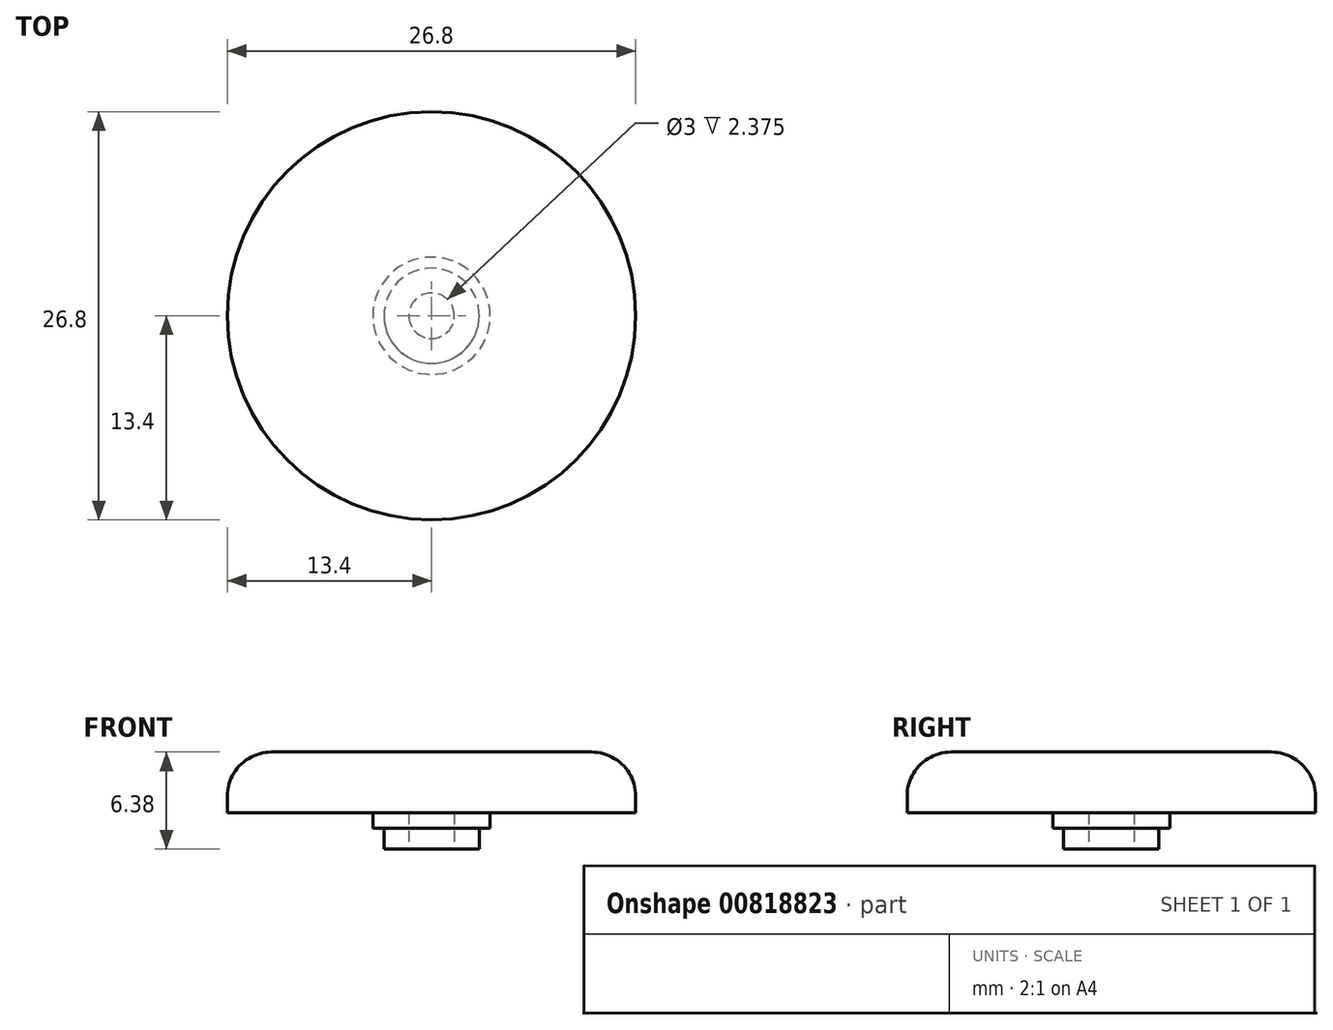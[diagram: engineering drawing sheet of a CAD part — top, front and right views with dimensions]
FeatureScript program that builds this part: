
annotation { "Feature Type Name" : "Feature", "Feature Type Description" : "" }
export const myFeature = defineFeature(function(context is Context, id is Id, definition is map)
    precondition{}
    {
        {
            var Q0;
            Q0=qCreatedBy(makeId("Top.planeOp"),FACE);
            var sketch = newSketch(context, id + "F0", { "sketchPlane" : qUnion([Q0])});
            skCircle(sketch, "E0", {"center": v(0, 0) * mm, "radius": 3.13 * mm});
            skCircle(sketch, "E1", {"center": v(0, 0) * mm, "radius": 1.5 * mm});
            skSolve(sketch);
        }
        {
            var Q0;
            Q0=makeQuery(id+"F0.imprint","IMPRINT",FACE,{"disambiguationData":[TD([[makeQuery(id+"F0.imprint","IMPRINT",EDGE,{"derivedFrom":sQuery(id+"F0.wireOp",EDGE,"E0")}),1.0]])]});
            extrude(context, id + "F1", {"entities" : qUnion([Q0]), "depth" : 2.38 * mm, "offsetDistance" : 25 * mm});
        }
        {
            var Q0;
            Q0=makeQuery(id+"F1.opExtrude","CAP_FACE",FACE,{"disambiguationData":[OSD([sQuery(id+"F0.wireOp",EDGE,"E0")])],"isStart":false});
            var sketch = newSketch(context, id + "F2", { "sketchPlane" : qUnion([Q0])});
            skCircle(sketch, "E2", {"center": v(0, 0) * mm, "radius": 13.4 * mm});
            skSolve(sketch);
        }
        {
            var Q0;
            Q0=makeQuery(id+"F2.imprint","IMPRINT",FACE,{"disambiguationData":[TD([[makeQuery(id+"F2.imprint","IMPRINT",EDGE,{"derivedFrom":sQuery(id+"F2.wireOp",EDGE,"E2")}),1.0]])]});
            var Q1;
            Q1=makeQuery(id+"F2.imprint","IMPRINT",FACE,{"disambiguationData":[TD([[makeQuery(id+"F2.imprint","IMPRINT",EDGE,{"derivedFrom":makeQuery(id+"F1.opExtrude","CAP_EDGE",EDGE,{"disambiguationData":[OSD([sQuery(id+"F0.wireOp",EDGE,"E0")])],"isStart":false})}),1.0]])]});
            extrude(context, id + "F3", {"entities" : qUnion([Q0, Q1]), "depth" : 4 * mm, "offsetDistance" : 25 * mm});
        }
        {
            var Q0;
            Q0=makeQuery(id+"F3.opExtrude","CAP_EDGE",EDGE,{"disambiguationData":[OSD([sQuery(id+"F2.wireOp",EDGE,"E2")])],"isStart":false});
            fillet(context, id + "F4", {"entities" : qUnion([Q0]), "radius" : 2.9 * mm, "tangentPropagation" : true, "allowEdgeOverflow" : false});
        }
        {
            var Q0;
            Q0=makeQuery(id+"F3.opExtrude","CAP_FACE",FACE,{"disambiguationData":[OSD([sQuery(id+"F2.wireOp",EDGE,"E2")])],"isStart":true});
            var sketch = newSketch(context, id + "F5", { "sketchPlane" : qUnion([Q0])});
            skCircle(sketch, "E3", {"center": v(0, 0) * mm, "radius": 3.85 * mm});
            skSolve(sketch);
        }
        {
            var Q0;
            Q0=makeQuery(id+"F5.imprint","IMPRINT",FACE,{"disambiguationData":[TD([[makeQuery(id+"F5.imprint","IMPRINT",EDGE,{"derivedFrom":sQuery(id+"F5.wireOp",EDGE,"E3")}),1.0]])]});
            extrude(context, id + "F6", {"entities" : qUnion([Q0]), "depth" : 1 * mm, "offsetDistance" : 25 * mm});
        }
        {
            var Q0;
            Q0=makeQuery(id+"F5.imprint","IMPRINT",FACE,{"disambiguationData":[TD([[makeQuery(id+"F5.imprint","IMPRINT",EDGE,{"derivedFrom":makeQuery(id+"F3.opExtrude","CAP_EDGE",EDGE,{"disambiguationData":[OSD([sQuery(id+"F0.wireOp",EDGE,"E1")])],"isStart":true})}),-1.0]])]});
            extrude(context, id + "F7", {"entities" : qUnion([Q0]), "operationType" : NewBodyOperationType.ADD, "oppositeDirection" : true, "depth" : 4 * mm, "offsetDistance" : 25 * mm});
        }
    });
